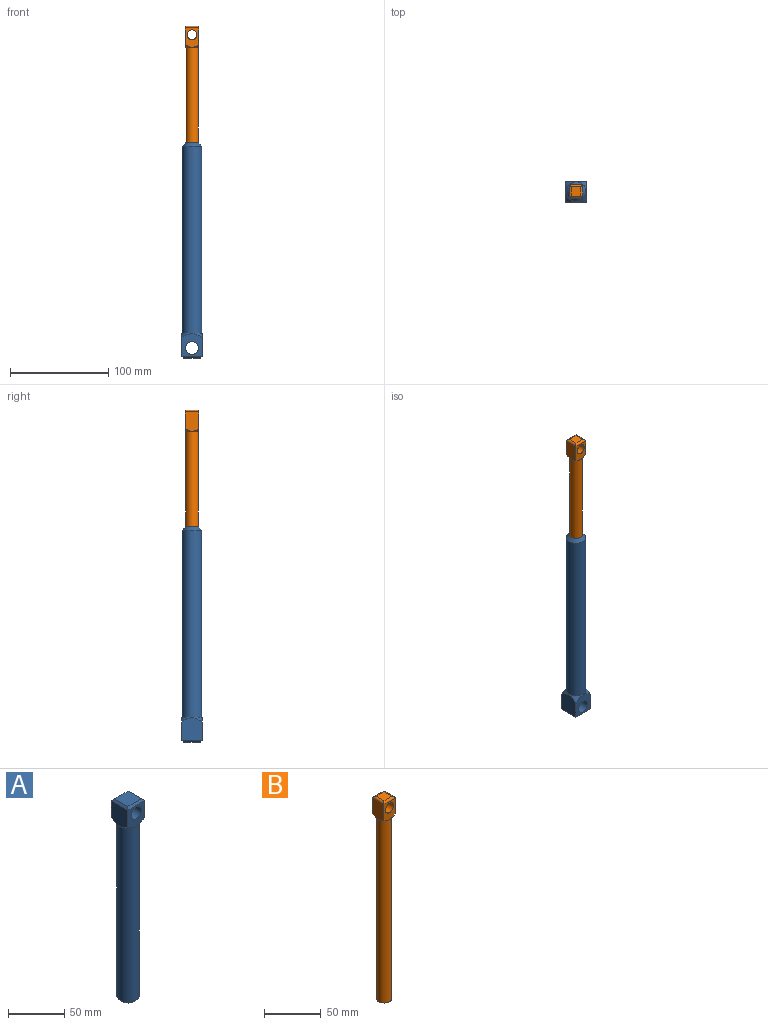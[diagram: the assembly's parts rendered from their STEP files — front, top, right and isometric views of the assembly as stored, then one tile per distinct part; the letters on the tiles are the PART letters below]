
ASSEMBLY  parts=2 mates=1
PART A: 15 faces, bbox 29.8x29.8x218.8 mm
  f0: cylinder r=6.5mm len=198.5mm, axis (0,0,-1), area 8106.9mm2, adj f7,f14
  f1: cylinder r=10mm len=190mm, axis (0,0,-1), area 11938.1mm2, adj f9,f14
  f2: plane 17.16x16.84mm, normal (0,0,1), area 289.1mm2, adj f10,f11,f12,f13
  f3: plane 22.59x20.84mm, normal (-1,0,0), area 439mm2, adj f4,f6,f9,f13
  f4: plane 22.75x21.16mm, normal (0,1,0), area 315mm2, adj f3,f5,f8,f9,f12
  f5: plane 22.69x20.95mm, normal (1,0,0), area 439mm2, adj f4,f6,f9,f10
  f6: plane 22.75x21.16mm, normal (0,-1,0), area 315mm2, adj f3,f5,f8,f9,f11
  f7: plane 13x13mm, normal (0,0,-1), area 132.7mm2, adj f0
  f8: cylinder r=6.5mm len=20.84mm, axis (0,1,0), area 851.3mm2, adj f4,f6
  f9: cone r=15mm half-angle=45deg, axis (0,0,1), area 179.6mm2, adj f1,f3,f4,f5,f6
  f10: plane 20.84x2mm, normal (0.71,0,0.71), area 53.3mm2, adj f2,f5,f11,f12
  f11: plane 21.16x2mm, normal (0,-0.71,0.71), area 54.2mm2, adj f2,f6,f10,f13
  f12: plane 21.16x2mm, normal (0,0.71,0.71), area 54.2mm2, adj f2,f4,f10,f13
  f13: plane 20.84x2mm, normal (-0.71,0,0.71), area 53.3mm2, adj f2,f3,f11,f12
  f14: cone r=10mm half-angle=45deg, axis (0,0,1), area 256.6mm2, adj f0,f1
PART B: 13 faces, bbox 19.5x19.5x218.1 mm
  f0: cylinder r=6.5mm len=196mm, axis (0,0,-1), area 8004.8mm2, adj f1,f8
  f1: plane 13x13mm, normal (0,0,-1), area 132.7mm2, adj f0
  f2: plane 19.64x13.78mm, normal (0,-1,0), area 177.9mm2, adj f3,f5,f7,f8,f9
  f3: plane 19.69x13.8mm, normal (1,0,0), area 255.4mm2, adj f2,f4,f8,f10
  f4: plane 19.64x13.78mm, normal (0,1,0), area 177.9mm2, adj f3,f5,f7,f8,f12
  f5: plane 19.61x13.73mm, normal (-1,0,0), area 255.4mm2, adj f2,f4,f8,f11
  f6: plane 9.78x9.73mm, normal (0,0,1), area 95.1mm2, adj f9,f10,f11,f12
  f7: cylinder r=5mm len=13.73mm, axis (0,1,0), area 431.3mm2, adj f2,f4
  f8: cone r=10.5mm half-angle=45deg, axis (0,0,1), area 79.9mm2, adj f0,f2,f3,f4,f5
  f9: cylinder r=2mm len=13.78mm, axis (-1,0,0), area 38.7mm2, adj f2,f6,f10,f11
  f10: cylinder r=2mm len=13.73mm, axis (0,-1,0), area 38.6mm2, adj f3,f6,f9,f12
  f11: cylinder r=2mm len=13.73mm, axis (0,1,0), area 38.6mm2, adj f5,f6,f9,f12
  f12: cylinder r=2mm len=13.78mm, axis (1,0,0), area 38.7mm2, adj f4,f6,f10,f11
PLACE A rot(axis=(1,0,0),180deg) t=(-122.7,112.82,219.61)mm
PLACE B t=(-99.03,69.11,118.86)mm
MATE slider B.f0 <-> A.f0  axis (0,0,-1) through (-122.7,112.82,118.86)mm
